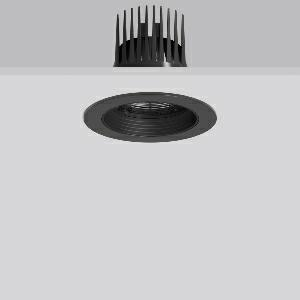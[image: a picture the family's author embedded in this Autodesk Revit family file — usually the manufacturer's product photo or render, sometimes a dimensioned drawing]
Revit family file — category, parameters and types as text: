
# Revit family: heledon_maxi_e_901760_003_2_6298
name_source: partatom
category: Lighting Fixtures
units: mm (PartAtom-declared; Revit-internal decimal feet)

## family parameters
Cut with Voids When Loaded = No
Host = Face
Light Source = No
Part Type = Normal
Room Calculation Point = No
Round Connector Dimension = Use Diameter
Shared = No

## types (1)
- HELEDON maxi E (1 x LED Modul 927, 2650 lm, 2700)
    Apparent Load = 25 VA
    Approval mark = CE
    CIE Flux Codes = 97 100 100 100 100
    Color Rendering = 92
    Color Temperature = 2700
    Default Elevation = 1800 mm
    Description = Series: HELEDON maxi
Round recessed downlight. Housing: die-cast aluminium, powder-coated. Black plastic ring and recessed LED to prevent glare from the side. Optical assembly with lens made of plastic (polycarbonate) for the best homogeneous light distribution - can be changed without tools. Best colour rendering index Ra>90. Suitable for Recessed ceiling mounting. Installation without tools thanks to spring fastening system. Including separate LED converter with connecting cable 600 mm.High quality converter without flickering and stroboscopic effect. Through-wiring box (5 pole) available as accessory. The following accessories can be mounted without use of tools: interchangeable lenses, decorative glasses, honeycomb louvre, clear and frosted diffusers, white interchangeable plastic ring. 
Colour: deep black, matt (RAL 9005)
Diameter: 162 mm
Height: 3 mm
Cut-out diameter: 152 mm
Recess height: 200 mm
Luminaire: recess height: 135 mm
Lamp: LED
Socket: without socket
Colour temperature: 2700K
Colour rendering index (CRI): 92
System power: 25 W
Rated luminous flux: 2650 lm
Luminous efficiency: 106 lm/W
Control gear: Regulated power supply
Protection class: II
Type of protection: IP 20
    Height = 0 mm  [stored 0 ft]
    Lamp = 1 x LED Modul 927
    Lamp Light Flux = 2650 lm
    Lamp count = 1
    Length = 162 mm
    Lifetime = 50000 h
    Luminous efficacy = 106 lm/W
    Manufacturer = RZB
    ModVariant = No
    Model = 901760.003.2
    Mounting Place = Ceiling
    Mounting Type = Recessed
    Number of Poles = 1
    OnlyDefault = Yes
    Power Factor = 1
    Product Name = HELEDON maxi E
    Product group = Recessed downlights
    ProductGroupID = 402
    Protection Class = Protection class II
    Protection Degree = IP 20
    RLX_Detail_Level = 1
    RLX_Emergency_Light_Flux = 0 lm
    RLX_Emergency_Type = 0
    RLX_Emergency_Type_DB = No
    RlxData = <blob elided: 121305 chars, md5=8a729597>
    Socket = socket
    Standby Power = 0 W
    System Light Flux = 2650 lm
    System Power = 25 W
    Type Comments = Product without accessories
    Type Image = 901663.003.jpg
    URL = http://relux.com
    VarID = ---
    Voltage = 230 V
    Voltage Range = 220-240 V
    Weight = 0.00 kg
    Width = 0 mm  [stored 0 ft]

note: [stored X ft] marks values corroborated as IEEE doubles in the binary element streams (Revit-internal decimal feet)

## geometry (parser evidence)
native form markers: Blend x4, Sweep x10
no freeform markers — native parametric forms only
